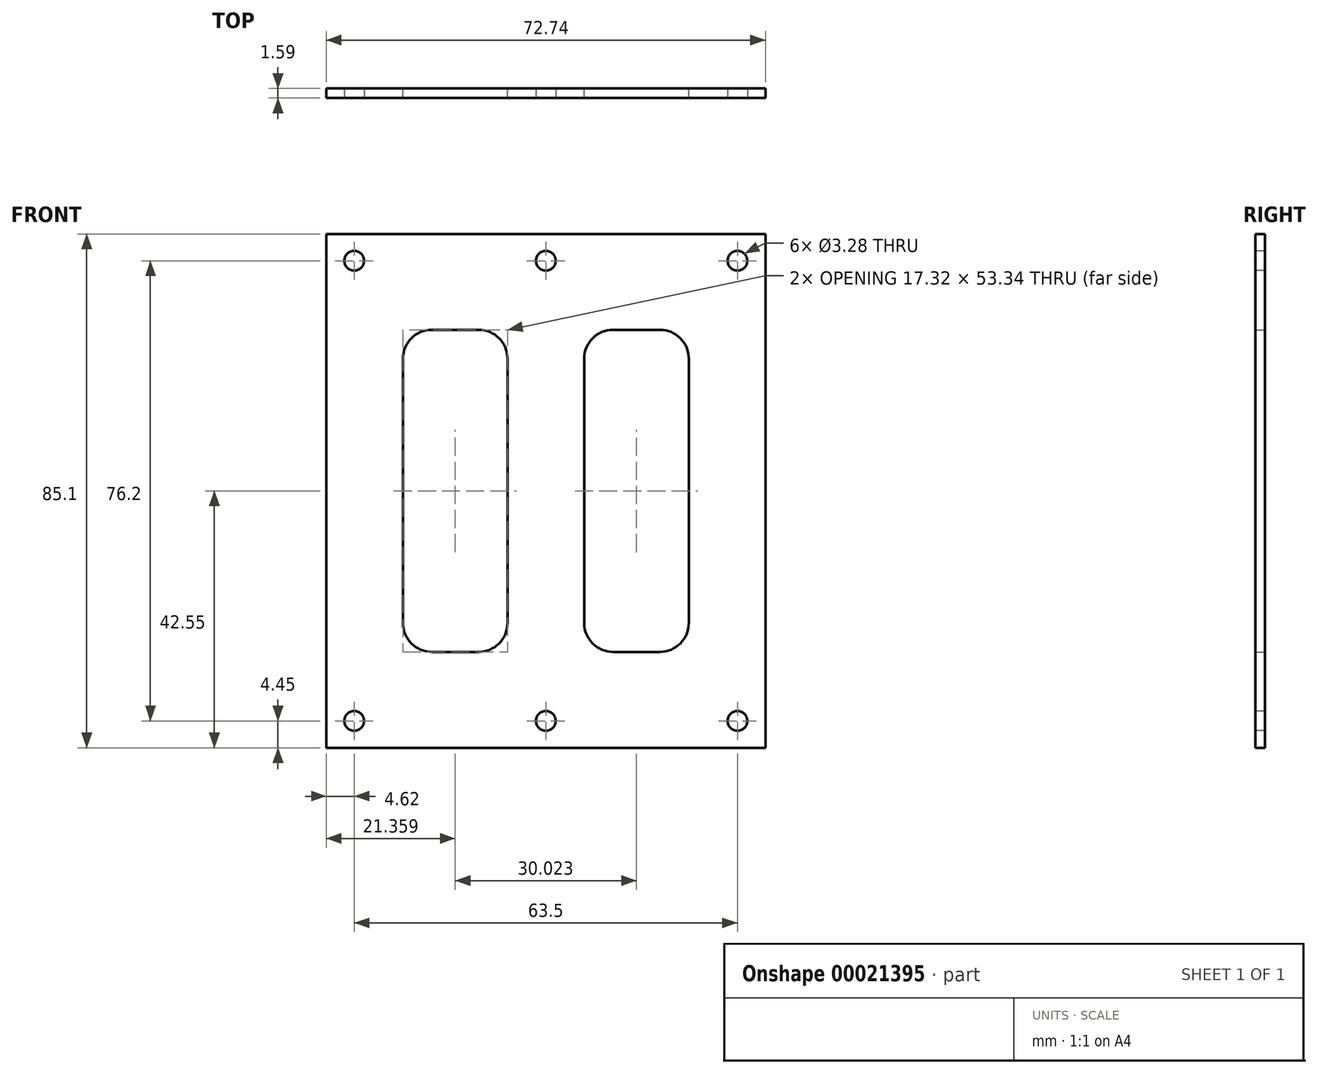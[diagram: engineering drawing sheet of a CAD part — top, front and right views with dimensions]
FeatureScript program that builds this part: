
annotation { "Feature Type Name" : "Feature", "Feature Type Description" : "" }
export const myFeature = defineFeature(function(context is Context, id is Id, definition is map)
    precondition{}
    {
        {
            var Q0;
            Q0=qCreatedBy(makeId("Front.planeOp"),FACE);
            var sketch = newSketch(context, id + "F0", { "sketchPlane" : qUnion([Q0])});
            skLineSegment(sketch, "E0.rect.bottom", {"start": v(36.37, 42.54) * mm, "end": v(-36.37, 42.55) * mm});
            skLineSegment(sketch, "E0.rect.top", {"start": v(36.37, -42.55) * mm, "end": v(-36.37, -42.55) * mm});
            skLineSegment(sketch, "E0.rect.left", {"start": v(36.37, 42.54) * mm, "end": v(36.37, -42.55) * mm});
            skLineSegment(sketch, "E0.rect.right", {"start": v(-36.37, 42.55) * mm, "end": v(-36.37, -42.54) * mm});
            skLineSegment(sketch, "E1", {"start": v(0, 0) * mm, "end": v(0, 81.51) * mm});
            skLineSegment(sketch, "E2.bottom", {"start": v(-23.67, 26.67) * mm, "end": v(-6.35, 26.67) * mm});
            skLineSegment(sketch, "E2.top", {"start": v(-23.67, -26.67) * mm, "end": v(-6.35, -26.67) * mm});
            skLineSegment(sketch, "E2.left", {"start": v(-23.67, 26.67) * mm, "end": v(-23.67, -26.67) * mm});
            skLineSegment(sketch, "E2.right", {"start": v(-6.35, 26.67) * mm, "end": v(-6.35, -26.67) * mm});
            skLineSegment(sketch, "E3.bottom", {"start": v(6.35, 26.67) * mm, "end": v(23.67, 26.67) * mm});
            skLineSegment(sketch, "E3.top", {"start": v(6.35, -26.67) * mm, "end": v(23.67, -26.67) * mm});
            skLineSegment(sketch, "E3.left", {"start": v(6.35, 26.67) * mm, "end": v(6.35, -26.67) * mm});
            skLineSegment(sketch, "E3.right", {"start": v(23.67, 26.67) * mm, "end": v(23.67, -26.67) * mm});
            skLineSegment(sketch, "E4", {"start": v(0, 0) * mm, "end": v(38.16, 0) * mm});
            skSolve(sketch);
        }
        {
            var Q0;
            {var subQ13=sQuery(id+"F0.wireOp",EDGE,"E0.rect.top");Q0=makeQuery(id+"F0.imprint","IMPRINT",FACE,{"disambiguationData":[TD([[makeQuery(id+"F0.imprint","IMPRINT",EDGE,{"derivedFrom":subQ13}),-1.0]])]});}
            var Q1;
            {var subQ7=sQuery(id+"F0.wireOp",EDGE,"E3.bottom");Q1=makeQuery(id+"F0.imprint","IMPRINT",FACE,{"disambiguationData":[TD([[makeQuery(id+"F0.imprint","IMPRINT",EDGE,{"derivedFrom":subQ7}),1.0]])]});}
            extrude(context, id + "F1", {"entities" : qUnion([Q0, Q1]), "depth" : 1.59 * mm});
        }
        {
            var Q0;
            Q0=makeQuery(id+"F1.opExtrude","SWEPT_EDGE",EDGE,{"disambiguationData":[OSD([sQuery(id+"F0.wireOp",EDGE,"E3.bottom"),sQuery(id+"F0.wireOp",EDGE,"E3.left")])]});
            var Q1;
            Q1=makeQuery(id+"F1.opExtrude","SWEPT_EDGE",EDGE,{"disambiguationData":[OSD([sQuery(id+"F0.wireOp",EDGE,"E3.bottom"),sQuery(id+"F0.wireOp",EDGE,"E3.right")])]});
            var Q2;
            Q2=makeQuery(id+"F1.opExtrude","SWEPT_EDGE",EDGE,{"disambiguationData":[OSD([sQuery(id+"F0.wireOp",EDGE,"E3.top"),sQuery(id+"F0.wireOp",EDGE,"E3.right")])]});
            var Q3;
            Q3=makeQuery(id+"F1.opExtrude","SWEPT_EDGE",EDGE,{"disambiguationData":[OSD([sQuery(id+"F0.wireOp",EDGE,"E2.top"),sQuery(id+"F0.wireOp",EDGE,"E2.left")])]});
            var Q4;
            Q4=makeQuery(id+"F1.opExtrude","SWEPT_EDGE",EDGE,{"disambiguationData":[OSD([sQuery(id+"F0.wireOp",EDGE,"E2.bottom"),sQuery(id+"F0.wireOp",EDGE,"E2.left")])]});
            var Q5;
            Q5=makeQuery(id+"F1.opExtrude","SWEPT_EDGE",EDGE,{"disambiguationData":[OSD([sQuery(id+"F0.wireOp",EDGE,"E2.bottom"),sQuery(id+"F0.wireOp",EDGE,"E2.right")])]});
            var Q6;
            Q6=makeQuery(id+"F1.opExtrude","SWEPT_EDGE",EDGE,{"disambiguationData":[OSD([sQuery(id+"F0.wireOp",EDGE,"E2.top"),sQuery(id+"F0.wireOp",EDGE,"E2.right")])]});
            var Q7;
            Q7=makeQuery(id+"F1.opExtrude","SWEPT_EDGE",EDGE,{"disambiguationData":[OSD([sQuery(id+"F0.wireOp",EDGE,"E3.top"),sQuery(id+"F0.wireOp",EDGE,"E3.left")])]});
            fillet(context, id + "F2", {"entities" : qUnion([Q0, Q1, Q2, Q3, Q4, Q5, Q6, Q7]), "radius" : 4.78 * mm, "tangentPropagation" : true, "allowEdgeOverflow" : false});
        }
        {
            var Q0;
            Q0=makeQuery(id+"F1.opExtrude","CAP_FACE",FACE,{"disambiguationData":[OSD([sQuery(id+"F0.wireOp",EDGE,"E0.rect.bottom"),sQuery(id+"F0.wireOp",EDGE,"E0.rect.top"),sQuery(id+"F0.wireOp",EDGE,"E0.rect.left"),sQuery(id+"F0.wireOp",EDGE,"E0.rect.right"),sQuery(id+"F0.wireOp",EDGE,"E2.bottom"),sQuery(id+"F0.wireOp",EDGE,"E2.top"),sQuery(id+"F0.wireOp",EDGE,"E2.left"),sQuery(id+"F0.wireOp",EDGE,"E2.right"),sQuery(id+"F0.wireOp",EDGE,"E3.bottom"),sQuery(id+"F0.wireOp",EDGE,"E3.top"),sQuery(id+"F0.wireOp",EDGE,"E3.left"),sQuery(id+"F0.wireOp",EDGE,"E3.right")])],"isStart":false});
            var sketch = newSketch(context, id + "F3", { "sketchPlane" : qUnion([Q0])});
            skLineSegment(sketch, "E5.rect.bottom", {"start": v(31.75, 38.1) * mm, "end": v(-31.75, 38.1) * mm});
            skLineSegment(sketch, "E5.rect.top", {"start": v(31.75, -38.1) * mm, "end": v(-31.75, -38.1) * mm});
            skLineSegment(sketch, "E5.rect.left", {"start": v(31.75, 38.1) * mm, "end": v(31.75, -38.1) * mm});
            skLineSegment(sketch, "E5.rect.right", {"start": v(-31.75, 38.1) * mm, "end": v(-31.75, -38.1) * mm});
            skPoint(sketch, "E5.rect.middle", {"position": v(0, 0) * mm});
            skLineSegment(sketch, "E6", {"start": v(0, 38.1) * mm, "end": v(0, -38.1) * mm});
            skSolve(sketch);
        }
        {
            var Q0;
            Q0=sQuery(id+"F3.wireOp",VERTEX,"E5.rect.right.start");
            var Q1;
            Q1=sQuery(id+"F3.wireOp",VERTEX,"E6.start");
            var Q2;
            Q2=sQuery(id+"F3.wireOp",VERTEX,"E5.rect.left.start");
            var Q3;
            Q3=sQuery(id+"F3.wireOp",VERTEX,"E5.rect.left.end");
            var Q4;
            Q4=sQuery(id+"F3.wireOp",VERTEX,"E6.end");
            var Q5;
            Q5=sQuery(id+"F3.wireOp",VERTEX,"E5.rect.top.end");
            var Q6;
            Q6=makeQuery(id+"F1.opExtrude","SWEPT_BODY",BODY,{"disambiguationData":[OSD([sQuery(id+"F0.wireOp",EDGE,"E0.rect.bottom"),sQuery(id+"F0.wireOp",EDGE,"E0.rect.top"),sQuery(id+"F0.wireOp",EDGE,"E0.rect.left"),sQuery(id+"F0.wireOp",EDGE,"E0.rect.right"),sQuery(id+"F0.wireOp",EDGE,"E2.bottom"),sQuery(id+"F0.wireOp",EDGE,"E2.top"),sQuery(id+"F0.wireOp",EDGE,"E2.left"),sQuery(id+"F0.wireOp",EDGE,"E2.right"),sQuery(id+"F0.wireOp",EDGE,"E3.bottom"),sQuery(id+"F0.wireOp",EDGE,"E3.top"),sQuery(id+"F0.wireOp",EDGE,"E3.left"),sQuery(id+"F0.wireOp",EDGE,"E3.right")])]});
            hole(context, id + "F4", {"style" : HoleStyle.SIMPLE, "holeDiameter" : 3.28 * mm, "endStyle" : HoleEndStyle.THROUGH, "locations" : qUnion([Q0, Q1, Q2, Q3, Q4, Q5]), "scope" : qUnion([Q6])});
        }
    });
